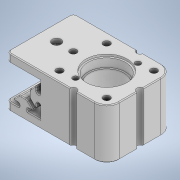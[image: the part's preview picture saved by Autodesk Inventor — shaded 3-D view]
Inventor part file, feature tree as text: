
AUTODESK INVENTOR PART (.ipt)
format: ipt  version: 2020 (Build 240168000, 168)  size: 509,952 bytes
history: native  units: in
note: dims shown in document units (in); Inventor stores cm internally (conversion verified against a paired STEP export)
features: reference x25, extrude x10, sketch x10, chamfer x4, other x2, plane x1, mirror x1, fillet x1
ambient origin geometry x8: Origin, YZ Plane, XZ Plane, XY Plane, X Axis, Y Axis, Z Axis, Center Point
bodies: Solid1 (feature_tree)
feature tree (54):
  extrude  "Extrusion1"  Depth=0.0098in
  extrude  "Extrusion2"  Depth=1.0in
  extrude  "Extrusion3"  Depth=2.0in TaperAngle=0.0deg
  extrude  "Extrusion4"  Depth=0.5in
  extrude  "Extrusion5"  Depth=0.3937in
  plane  "Work Plane1"
  mirror  "Mirror1"
  extrude  "Extrusion6"  Depth=1.0in
  fillet  "Fillet1"  Radius=1.0in
  extrude  "Extrusion7"  TaperAngle=0.0deg  [1 undecoded]
  chamfer  "Chamfer1"  Distance=0.314in
  chamfer  "Chamfer2"  Distance=0.064in
  chamfer  "Chamfer3"  Distance=1.0in
  extrude  "Extrusion8"  Depth=0.125in TaperAngle=360.0deg
  extrude  "Extrusion9"  TaperAngle=0.0deg  [1 undecoded]
  chamfer  "Chamfer4"  Distance=0.375in
  extrude  "Extrusion10"  Depth=0.125in
  sketch  "Sketch1"  dims[d0=0.0098in d1=0.0098in]
  reference  "Reference1"
  reference  "Reference2"
  reference  "Reference3"
  reference  "Reference4"
  reference  "Reference5"
  reference  "Reference6"
  reference  "Reference7"
  reference  "Reference8"
  reference  "Reference9"
  reference  "Reference10"
  reference  "Reference11"
  reference  "Reference12"
  reference  "Reference13"
  reference  "Reference14"
  reference  "Reference15"
  reference  "Reference16"
  reference  "Reference17"
  reference  "Reference18"
  reference  "Reference19"
  reference  "Reference20"
  reference  "Reference21"
  reference  "Reference22"
  reference  "Reference23"
  reference  "Reference24"
  reference  "Reference25"
  sketch  "Sketch2"  dims[d2=0.25in d3=1.0in]
  sketch  "Sketch4"  dims[d4=2.0in d5=2.0in d6=0.0in]
  sketch  "Sketch5"  dims[d7=0.5in d8=0.5in]
  sketch  "Sketch6"  dims[d9=0.2656in d10=1.1811in d12=0.5in d13=0.3937in d15=1.0in]
  sketch  "Sketch7"  dims[d17=0.5in d18=0.0in d19=1.024in d20=1.0in]
  sketch  "Sketch8"  dims[d21=1.0in d22=0.0in d23=0.0in]
  sketch  "Sketch10"  dims[d24=1.125in d25=0.314in d26=0.0in]
  sketch  "Sketch12"  dims[d27=1.226in d28=0.064in d29=0.0in]
  sketch  "Sketch13"  dims[d30=0.2in d31=1.0in d32=3.1496in d34=360.0deg d36=0.0in d37=0.0in d38=0.375in d39=1.429in d40=0.165in d41=67.5deg d42=0.0in d43=0.0in d44=0.025in d45=0.125in d46=45.0deg d47=0.125in d48=0.025in d49=0.125in d50=45.0deg d51=0.025in d52=0.125in d53=45.0deg d54=0.6in d55=1.25in d56=0.0in d57=0.61in d58=0.5in d59=0.0in d60=0.31in d61=0.125in d62=45.0deg d63=0.125in d64=0.0in]
  other  "Assembly3"
  other  "1003-9-CL:1"
note: 2 required parameter values undecoded (feature->parameter linkage not recoverable at this tier; creation-order binding heuristic only, values carry confidence <= 0.55)
